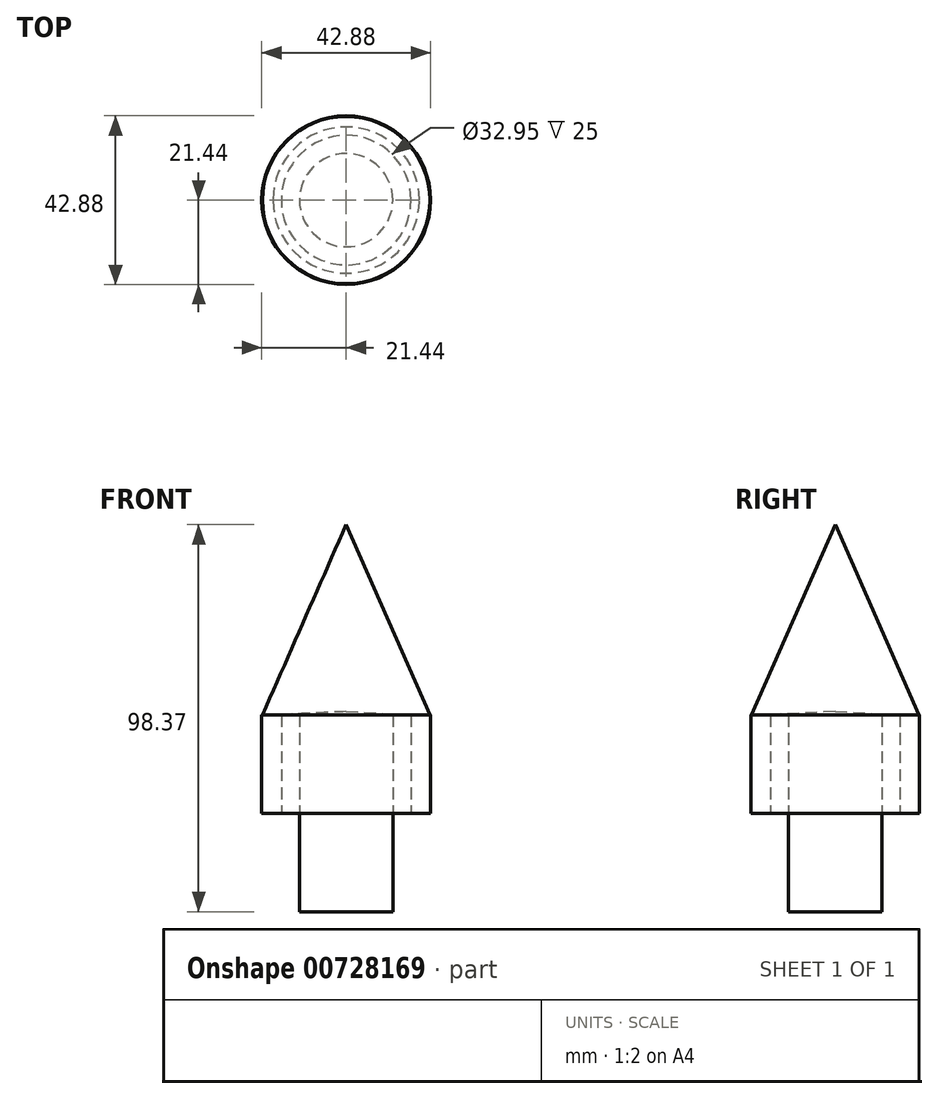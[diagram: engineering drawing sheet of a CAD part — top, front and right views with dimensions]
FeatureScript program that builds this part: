
annotation { "Feature Type Name" : "Feature", "Feature Type Description" : "" }
export const myFeature = defineFeature(function(context is Context, id is Id, definition is map)
    precondition{}
    {
        {
            var Q0;
            Q0=qCreatedBy(makeId("Top.planeOp"),FACE);
            var sketch = newSketch(context, id + "F0", { "sketchPlane" : qUnion([Q0])});
            skCircle(sketch, "E0", {"center": v(0, 0) * mm, "radius": 21.44 * mm});
            skCircle(sketch, "E1", {"center": v(0, 0) * mm, "radius": 19.35 * mm});
            skSolve(sketch);
        }
        {
            var Q0;
            Q0=qSketchRegion(id+"F0",true);
            extrude(context, id + "F1", {"entities" : qUnion([Q0]), "depth" : 25 * mm, "offsetDistance" : 25 * mm});
        }
        {
            var Q0;
            Q0=qCreatedBy(makeId("Right.planeOp"),FACE);
            var sketch = newSketch(context, id + "F2", { "sketchPlane" : qUnion([Q0])});
            skLineSegment(sketch, "E2", {"start": v(-21.31, 24.87) * mm, "end": v(0, 73.37) * mm});
            skLineSegment(sketch, "E3", {"start": v(0, 73.37) * mm, "end": v(0, 25.87) * mm});
            skLineSegment(sketch, "E4", {"start": v(0, 25.87) * mm, "end": v(-21.31, 24.87) * mm});
            skLineSegment(sketch, "E5", {"start": v(0, 0) * mm, "end": v(0, 12.37) * mm});
            skSolve(sketch);
        }
        {
            var Q0;
            Q0=qSketchRegion(id+"F2",true);
            var Q1;
            Q1=sQuery(id+"F2.wireOp",EDGE,"E5");
            revolve(context, id + "F3", {"operationType" : NewBodyOperationType.ADD, "surfaceOperationType" : NewSurfaceOperationType.NEW, "entities" : qUnion([Q0]), "axis" : qUnion([Q1]), "revolveType" : RevolveType.FULL});
        }
        {
            var Q0;
            Q0=qCreatedBy(makeId("Top.planeOp"),FACE);
            var sketch = newSketch(context, id + "F4", { "sketchPlane" : qUnion([Q0])});
            skCircle(sketch, "E6", {"center": v(0, 0) * mm, "radius": 19.35 * mm});
            skCircle(sketch, "E7", {"center": v(0, 0) * mm, "radius": 16.48 * mm});
            skSolve(sketch);
        }
        {
            var Q0;
            Q0=qSketchRegion(id+"F4",true);
            extrude(context, id + "F5", {"entities" : qUnion([Q0]), "operationType" : NewBodyOperationType.ADD, "depth" : 25 * mm, "offsetDistance" : 25 * mm});
        }
        {
            var Q0;
            Q0=qCreatedBy(makeId("Top.planeOp"),FACE);
            var sketch = newSketch(context, id + "F6", { "sketchPlane" : qUnion([Q0])});
            skCircle(sketch, "E8", {"center": v(0, 0) * mm, "radius": 11.86 * mm});
            skSolve(sketch);
        }
        {
            var Q0;
            Q0=makeQuery(id+"F6.imprint","IMPRINT",FACE,{"disambiguationData":[TD([[makeQuery(id+"F6.imprint","IMPRINT",EDGE,{"derivedFrom":sQuery(id+"F6.wireOp",EDGE,"E8")}),1.0]])]});
            extrude(context, id + "F7", {"entities" : qUnion([Q0]), "depth" : 25 * mm, "offsetDistance" : 25 * mm});
        }
        {
            var Q0;
            Q0=makeQuery(id+"F7.opExtrude","CAP_FACE",FACE,{"disambiguationData":[OSD([sQuery(id+"F6.wireOp",EDGE,"E8")])],"isStart":true});
            extrude(context, id + "F8", {"entities" : qUnion([Q0]), "operationType" : NewBodyOperationType.ADD, "depth" : 25 * mm, "offsetDistance" : 25 * mm});
        }
    });
